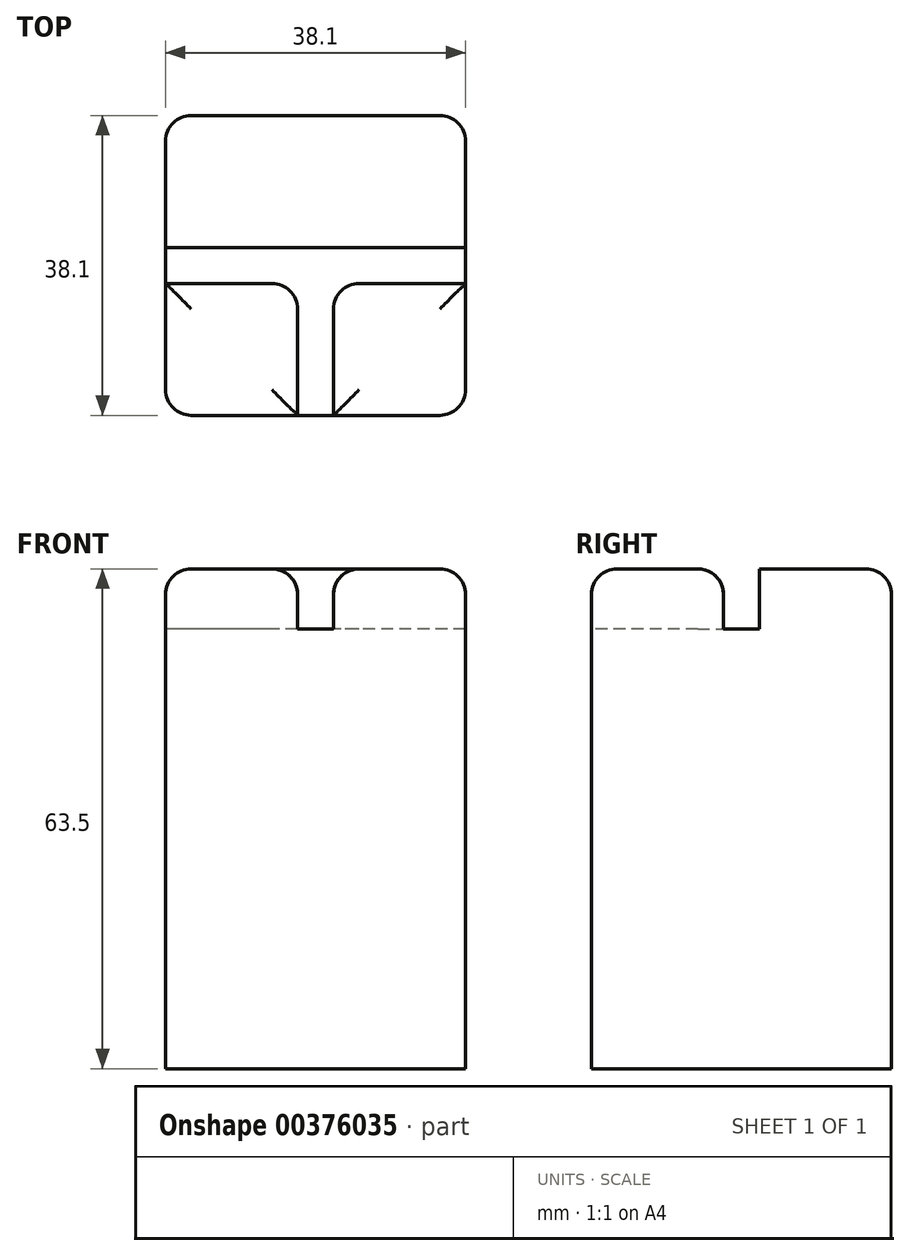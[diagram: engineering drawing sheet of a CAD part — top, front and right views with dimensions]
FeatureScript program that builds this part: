
annotation { "Feature Type Name" : "Feature", "Feature Type Description" : "" }
export const myFeature = defineFeature(function(context is Context, id is Id, definition is map)
    precondition{}
    {
        {
            var Q0;
            Q0=qCreatedBy(makeId("Top.planeOp"),FACE);
            var sketch = newSketch(context, id + "F0", { "sketchPlane" : qUnion([Q0])});
            skLineSegment(sketch, "E0.bottom", {"start": v(19.05, -19.05) * mm, "end": v(-19.05, -19.05) * mm});
            skLineSegment(sketch, "E0.top", {"start": v(19.05, 19.05) * mm, "end": v(-19.05, 19.05) * mm});
            skLineSegment(sketch, "E0.left", {"start": v(19.05, -19.05) * mm, "end": v(19.05, 19.05) * mm});
            skLineSegment(sketch, "E0.right", {"start": v(-19.05, -19.05) * mm, "end": v(-19.05, 19.05) * mm});
            skPoint(sketch, "E0.middle", {"position": v(0, 0) * mm});
            skSolve(sketch);
        }
        {
            var Q0;
            Q0=makeQuery(id+"F0.imprint","IMPRINT",FACE,{"disambiguationData":[TD([[makeQuery(id+"F0.imprint","IMPRINT",EDGE,{"derivedFrom":sQuery(id+"F0.wireOp",EDGE,"E0.bottom")}),-1.0]])]});
            var sketch = newSketch(context, id + "F1", { "sketchPlane" : qUnion([Q0])});
            skSolve(sketch);
        }
        {
            var Q0;
            Q0 = qSketchRegion(id + "F1", true);
            var Q1;
            Q1=makeQuery(id+"F0.imprint","IMPRINT",FACE,{"disambiguationData":[TD([[makeQuery(id+"F0.imprint","IMPRINT",EDGE,{"derivedFrom":sQuery(id+"F0.wireOp",EDGE,"E0.bottom")}),-1.0]])]});
            extrude(context, id + "F2", {"entities" : qUnion([Q0, Q1]), "endBound" : BoundingType.SYMMETRIC, "depth" : 63.5 * mm});
        }
        {
            var Q0;
            Q0=makeQuery(id+"F2.opExtrude","CAP_FACE",FACE,{"disambiguationData":[OSD([sQuery(id+"F0.wireOp",EDGE,"E0.bottom"),sQuery(id+"F0.wireOp",EDGE,"E0.top"),sQuery(id+"F0.wireOp",EDGE,"E0.left"),sQuery(id+"F0.wireOp",EDGE,"E0.right")])],"isStart":false});
            var sketch = newSketch(context, id + "F3", { "sketchPlane" : qUnion([Q0])});
            skLineSegment(sketch, "E1.bottom", {"start": v(19.05, -2.29) * mm, "end": v(-19.05, -2.29) * mm});
            skLineSegment(sketch, "E1.top", {"start": v(19.05, 2.29) * mm, "end": v(-19.05, 2.29) * mm});
            skLineSegment(sketch, "E1.left", {"start": v(19.05, -2.29) * mm, "end": v(19.05, 2.29) * mm});
            skLineSegment(sketch, "E1.right", {"start": v(-19.05, -2.29) * mm, "end": v(-19.05, 2.29) * mm});
            skPoint(sketch, "E1.middle", {"position": v(0, 0) * mm});
            skLineSegment(sketch, "E2.bottom", {"start": v(2.29, 19.05) * mm, "end": v(-2.29, 19.05) * mm});
            skLineSegment(sketch, "E2.top", {"start": v(2.29, -19.05) * mm, "end": v(-2.29, -19.05) * mm});
            skLineSegment(sketch, "E2.left", {"start": v(2.29, 19.05) * mm, "end": v(2.29, -19.05) * mm});
            skLineSegment(sketch, "E2.right", {"start": v(-2.29, 19.05) * mm, "end": v(-2.29, -19.05) * mm});
            skSolve(sketch);
        }
        {
            var Q0;
            {var subQ5=sQuery(id+"F3.wireOp",EDGE,"E2.bottom");Q0=makeQuery(id+"F3.imprint","IMPRINT",FACE,{"disambiguationData":[TD([[makeQuery(id+"F3.imprint","IMPRINT",EDGE,{"derivedFrom":subQ5}),1.0]])]});}
            var sketch = newSketch(context, id + "F4", { "sketchPlane" : qUnion([Q0])});
            skSolve(sketch);
        }
        {
            var Q0;
            {var subQ5=sQuery(id+"F3.wireOp",EDGE,"E2.bottom");Q0=makeQuery(id+"F4.imprint","IMPRINT",FACE,{"disambiguationData":[TD([[makeQuery(id+"F4.imprint","IMPRINT",EDGE,{"derivedFrom":makeQuery(id+"F3.imprint","IMPRINT",EDGE,{"derivedFrom":subQ5})}),1.0]])]});}
            var Q1;
            {var subQ0=sQuery(id+"F3.wireOp",EDGE,"E1.right");Q1=makeQuery(id+"F3.imprint","IMPRINT",FACE,{"disambiguationData":[TD([[makeQuery(id+"F3.imprint","IMPRINT",EDGE,{"derivedFrom":subQ0}),-1.0]])]});}
            var Q2;
            {var subQ0=sQuery(id+"F3.wireOp",EDGE,"E2.left");var subQ1=sQuery(id+"F3.wireOp",EDGE,"E1.bottom");var subQ2=makeQuery(id+"F3.imprint","INTERSECT",VERTEX,{"derivedFrom":[subQ1,subQ0]});Q2=makeQuery(id+"F3.imprint","IMPRINT",FACE,{"disambiguationData":[TD([[makeQuery(id+"F3.imprint","IMPRINT",EDGE,{"disambiguationData":[TD([[subQ2,-1.0]])],"derivedFrom":subQ1}),-1.0]])]});}
            var Q3;
            {var subQ0=sQuery(id+"F3.wireOp",EDGE,"E1.left");Q3=makeQuery(id+"F3.imprint","IMPRINT",FACE,{"disambiguationData":[TD([[makeQuery(id+"F3.imprint","IMPRINT",EDGE,{"derivedFrom":subQ0}),1.0]])]});}
            var Q4;
            {var subQ5=sQuery(id+"F3.wireOp",EDGE,"E2.top");Q4=makeQuery(id+"F3.imprint","IMPRINT",FACE,{"disambiguationData":[TD([[makeQuery(id+"F3.imprint","IMPRINT",EDGE,{"derivedFrom":subQ5}),-1.0]])]});}
            extrude(context, id + "F5", {"entities" : qUnion([Q0, Q1, Q2, Q3, Q4]), "operationType" : NewBodyOperationType.REMOVE, "oppositeDirection" : true, "depth" : 7.62 * mm});
        }
        {
            var Q0;
            {var subQ0=sQuery(id+"F0.wireOp",EDGE,"E0.left");var subQ1=sQuery(id+"F0.wireOp",EDGE,"E0.top");var subQ3=makeQuery(id+"F2.opExtrude","CAP_EDGE",EDGE,{"disambiguationData":[OSD([subQ1])],"isStart":false});Q0=makeQuery(id+"F5.boolean.opBoolean","SPLIT",EDGE,{"disambiguationData":[TD([makeQuery(id+"F2.opExtrude","SWEPT_FACE",FACE,{"disambiguationData":[OSD([subQ0])]})])],"derivedFrom":subQ3});}
            var Q1;
            {var subQ1=sQuery(id+"F0.wireOp",EDGE,"E0.left");var subQ2=sQuery(id+"F0.wireOp",EDGE,"E0.top");var subQ6=makeQuery(id+"F2.opExtrude","CAP_EDGE",EDGE,{"disambiguationData":[OSD([subQ1])],"isStart":false});Q1=makeQuery(id+"F5.boolean.opBoolean","SPLIT",EDGE,{"disambiguationData":[TD([makeQuery(id+"F2.opExtrude","SWEPT_FACE",FACE,{"disambiguationData":[OSD([subQ2])]})])],"derivedFrom":subQ6});}
            var Q2;
            Q2=makeQuery(id+"F2.opExtrude","SWEPT_EDGE",EDGE,{"disambiguationData":[OSD([sQuery(id+"F0.wireOp",EDGE,"E0.top"),sQuery(id+"F0.wireOp",EDGE,"E0.left")])]});
            var Q3;
            {var subQ0=sQuery(id+"F3.wireOp",EDGE,"E2.left");Q3=makeQuery(id+"F5.boolean.opBoolean","COPY",EDGE,{"derivedFrom":makeQuery(id+"F5.opExtrude","CAP_EDGE",EDGE,{"disambiguationData":[OSD([subQ0]),TDD([makeQuery(id+"F4.imprint","IMPRINT",EDGE,{"derivedFrom":makeQuery(id+"F3.imprint","IMPRINT",EDGE,{"disambiguationData":[TD([[makeQuery(id+"F3.imprint","INTERSECT",VERTEX,{"derivedFrom":[sQuery(id+"F3.wireOp",EDGE,"E1.top"),subQ0]}),1.0]])],"derivedFrom":subQ0})})])],"isStart":true})});}
            var Q4;
            {var subQ1=sQuery(id+"F0.wireOp",EDGE,"E0.left");var subQ3=sQuery(id+"F3.wireOp",EDGE,"E1.top");var subQ4=makeQuery(id+"F3.imprint","INTERSECT",VERTEX,{"derivedFrom":[subQ3,sQuery(id+"F3.wireOp",EDGE,"E2.right")]});var subQ5=makeQuery(id+"F3.imprint","IMPRINT",EDGE,{"disambiguationData":[TD([[subQ4,-1.0]])],"derivedFrom":subQ3});var subQ6=sQuery(id+"F3.wireOp",EDGE,"E2.left");var subQ7=makeQuery(id+"F3.imprint","INTERSECT",VERTEX,{"derivedFrom":[subQ3,subQ6]});var subQ8=makeQuery(id+"F3.imprint","IMPRINT",EDGE,{"disambiguationData":[TD([[subQ7,-1.0]])],"derivedFrom":subQ3});var subQ9=makeQuery(id+"F3.imprint","IMPRINT",EDGE,{"disambiguationData":[TD([[subQ7,1.0]])],"derivedFrom":subQ3});Q4=makeQuery(id+"F5.boolean.opBoolean","COPY",EDGE,{"disambiguationData":[TD([makeQuery(id+"F2.opExtrude","SWEPT_FACE",FACE,{"disambiguationData":[OSD([subQ1])]})])],"derivedFrom":makeQuery(id+"F5.opExtrude","CAP_EDGE",EDGE,{"disambiguationData":[OSD([subQ3]),TDD([subQ9,subQ8,subQ5])],"isStart":true})});}
            var Q5;
            Q5=makeQuery(id+"F5.boolean.opBoolean","COPY",EDGE,{"derivedFrom":makeQuery(id+"F5.opExtrude","CAP_EDGE",EDGE,{"disambiguationData":[OSD([sQuery(id+"F3.wireOp",EDGE,"E1.left")])],"isStart":false})});
            var Q6;
            Q6=makeQuery(id+"F5.boolean.opBoolean","COPY",EDGE,{"derivedFrom":makeQuery(id+"F5.opExtrude","SWEPT_EDGE",EDGE,{"disambiguationData":[OSD([sQuery(id+"F0.wireOp",EDGE,"E0.left"),sQuery(id+"F3.wireOp",EDGE,"E1.top"),sQuery(id+"F3.wireOp",EDGE,"E1.left")])]})});
            var Q7;
            Q7=makeQuery(id+"F5.boolean.opBoolean","COPY",EDGE,{"derivedFrom":makeQuery(id+"F5.opExtrude","SWEPT_EDGE",EDGE,{"disambiguationData":[OSD([sQuery(id+"F0.wireOp",EDGE,"E0.left"),sQuery(id+"F3.wireOp",EDGE,"E1.bottom"),sQuery(id+"F3.wireOp",EDGE,"E1.left")])]})});
            var Q8;
            {var subQ0=sQuery(id+"F0.wireOp",EDGE,"E0.bottom");var subQ2=sQuery(id+"F0.wireOp",EDGE,"E0.left");var subQ3=makeQuery(id+"F2.opExtrude","CAP_EDGE",EDGE,{"disambiguationData":[OSD([subQ2])],"isStart":false});Q8=makeQuery(id+"F5.boolean.opBoolean","SPLIT",EDGE,{"disambiguationData":[TD([makeQuery(id+"F2.opExtrude","SWEPT_FACE",FACE,{"disambiguationData":[OSD([subQ0])]})])],"derivedFrom":subQ3});}
            var Q9;
            Q9=makeQuery(id+"F2.opExtrude","SWEPT_EDGE",EDGE,{"disambiguationData":[OSD([sQuery(id+"F0.wireOp",EDGE,"E0.bottom"),sQuery(id+"F0.wireOp",EDGE,"E0.left")])]});
            var Q10;
            {var subQ0=sQuery(id+"F0.wireOp",EDGE,"E0.bottom");var subQ1=sQuery(id+"F0.wireOp",EDGE,"E0.left");var subQ3=makeQuery(id+"F2.opExtrude","CAP_EDGE",EDGE,{"disambiguationData":[OSD([subQ0])],"isStart":false});Q10=makeQuery(id+"F5.boolean.opBoolean","SPLIT",EDGE,{"disambiguationData":[TD([makeQuery(id+"F2.opExtrude","SWEPT_FACE",FACE,{"disambiguationData":[OSD([subQ1])]})])],"derivedFrom":subQ3});}
            var Q11;
            Q11=makeQuery(id+"F5.boolean.opBoolean","COPY",EDGE,{"derivedFrom":makeQuery(id+"F5.opExtrude","SWEPT_EDGE",EDGE,{"disambiguationData":[OSD([sQuery(id+"F0.wireOp",EDGE,"E0.bottom"),sQuery(id+"F3.wireOp",EDGE,"E2.top"),sQuery(id+"F3.wireOp",EDGE,"E2.left")])]})});
            var Q12;
            Q12=makeQuery(id+"F5.boolean.opBoolean","COPY",EDGE,{"derivedFrom":makeQuery(id+"F5.opExtrude","CAP_EDGE",EDGE,{"disambiguationData":[OSD([sQuery(id+"F3.wireOp",EDGE,"E2.top")])],"isStart":false})});
            var Q13;
            Q13=makeQuery(id+"F5.boolean.opBoolean","COPY",EDGE,{"derivedFrom":makeQuery(id+"F5.opExtrude","SWEPT_EDGE",EDGE,{"disambiguationData":[OSD([sQuery(id+"F0.wireOp",EDGE,"E0.bottom"),sQuery(id+"F3.wireOp",EDGE,"E2.top"),sQuery(id+"F3.wireOp",EDGE,"E2.right")])]})});
            var Q14;
            {var subQ0=sQuery(id+"F3.wireOp",EDGE,"E2.left");Q14=makeQuery(id+"F5.boolean.opBoolean","COPY",EDGE,{"derivedFrom":makeQuery(id+"F5.opExtrude","CAP_EDGE",EDGE,{"disambiguationData":[OSD([subQ0]),TDD([makeQuery(id+"F3.imprint","IMPRINT",EDGE,{"disambiguationData":[TD([[makeQuery(id+"F3.imprint","INTERSECT",VERTEX,{"derivedFrom":[sQuery(id+"F3.wireOp",EDGE,"E1.bottom"),subQ0]}),-1.0]])],"derivedFrom":subQ0})])],"isStart":true})});}
            var Q15;
            {var subQ0=sQuery(id+"F3.wireOp",EDGE,"E1.bottom");Q15=makeQuery(id+"F5.boolean.opBoolean","COPY",EDGE,{"derivedFrom":makeQuery(id+"F5.opExtrude","CAP_EDGE",EDGE,{"disambiguationData":[OSD([subQ0]),TDD([makeQuery(id+"F3.imprint","IMPRINT",EDGE,{"disambiguationData":[TD([[makeQuery(id+"F3.imprint","INTERSECT",VERTEX,{"derivedFrom":[subQ0,sQuery(id+"F3.wireOp",EDGE,"E2.left")]}),1.0]])],"derivedFrom":subQ0})])],"isStart":true})});}
            var Q16;
            {var subQ0=sQuery(id+"F0.wireOp",EDGE,"E0.bottom");var subQ1=sQuery(id+"F0.wireOp",EDGE,"E0.right");var subQ2=sQuery(id+"F3.wireOp",EDGE,"E1.bottom");var subQ3=sQuery(id+"F3.wireOp",EDGE,"E2.right");var subQ4=makeQuery(id+"F3.imprint","INTERSECT",VERTEX,{"derivedFrom":[subQ2,subQ3]});Q16=makeQuery(id+"F5.boolean.opBoolean","SPLIT",FACE,{"disambiguationData":[TD([makeQuery(id+"F5.opExtrude","SWEPT_FACE",FACE,{"disambiguationData":[OSD([subQ2]),TDD([makeQuery(id+"F3.imprint","IMPRINT",EDGE,{"disambiguationData":[TD([[subQ4,-1.0]])],"derivedFrom":subQ2})])]})])],"derivedFrom":makeQuery(id+"F2.opExtrude","CAP_FACE",FACE,{"disambiguationData":[OSD([subQ0,sQuery(id+"F0.wireOp",EDGE,"E0.top"),sQuery(id+"F0.wireOp",EDGE,"E0.left"),subQ1])],"isStart":false})});}
            var Q17;
            {var subQ0=sQuery(id+"F3.wireOp",EDGE,"E1.bottom");Q17=makeQuery(id+"F5.boolean.opBoolean","COPY",EDGE,{"derivedFrom":makeQuery(id+"F5.opExtrude","CAP_EDGE",EDGE,{"disambiguationData":[OSD([subQ0]),TDD([makeQuery(id+"F3.imprint","IMPRINT",EDGE,{"disambiguationData":[TD([[makeQuery(id+"F3.imprint","INTERSECT",VERTEX,{"derivedFrom":[subQ0,sQuery(id+"F3.wireOp",EDGE,"E2.right")]}),-1.0]])],"derivedFrom":subQ0})])],"isStart":true})});}
            var Q18;
            Q18=makeQuery(id+"F5.boolean.opBoolean","COPY",EDGE,{"derivedFrom":makeQuery(id+"F5.opExtrude","SWEPT_EDGE",EDGE,{"disambiguationData":[OSD([sQuery(id+"F0.wireOp",EDGE,"E0.right"),sQuery(id+"F3.wireOp",EDGE,"E1.bottom"),sQuery(id+"F3.wireOp",EDGE,"E1.right")])]})});
            var Q19;
            Q19=makeQuery(id+"F5.boolean.opBoolean","COPY",EDGE,{"derivedFrom":makeQuery(id+"F5.opExtrude","CAP_EDGE",EDGE,{"disambiguationData":[OSD([sQuery(id+"F3.wireOp",EDGE,"E1.right")])],"isStart":false})});
            var Q20;
            Q20=makeQuery(id+"F5.boolean.opBoolean","COPY",EDGE,{"derivedFrom":makeQuery(id+"F5.opExtrude","SWEPT_EDGE",EDGE,{"disambiguationData":[OSD([sQuery(id+"F0.wireOp",EDGE,"E0.right"),sQuery(id+"F3.wireOp",EDGE,"E1.top"),sQuery(id+"F3.wireOp",EDGE,"E1.right")])]})});
            var Q21;
            {var subQ0=sQuery(id+"F0.wireOp",EDGE,"E0.right");var subQ2=sQuery(id+"F0.wireOp",EDGE,"E0.top");var subQ4=makeQuery(id+"F2.opExtrude","CAP_EDGE",EDGE,{"disambiguationData":[OSD([subQ0])],"isStart":false});Q21=makeQuery(id+"F5.boolean.opBoolean","SPLIT",EDGE,{"disambiguationData":[TD([makeQuery(id+"F2.opExtrude","SWEPT_FACE",FACE,{"disambiguationData":[OSD([subQ2])]})])],"derivedFrom":subQ4});}
            var Q22;
            Q22=makeQuery(id+"F2.opExtrude","SWEPT_EDGE",EDGE,{"disambiguationData":[OSD([sQuery(id+"F0.wireOp",EDGE,"E0.top"),sQuery(id+"F0.wireOp",EDGE,"E0.right")])]});
            var Q23;
            {var subQ0=sQuery(id+"F0.wireOp",EDGE,"E0.right");var subQ1=sQuery(id+"F0.wireOp",EDGE,"E0.top");var subQ3=makeQuery(id+"F2.opExtrude","CAP_EDGE",EDGE,{"disambiguationData":[OSD([subQ1])],"isStart":false});Q23=makeQuery(id+"F5.boolean.opBoolean","SPLIT",EDGE,{"disambiguationData":[TD([makeQuery(id+"F2.opExtrude","SWEPT_FACE",FACE,{"disambiguationData":[OSD([subQ0])]})])],"derivedFrom":subQ3});}
            var Q24;
            {var subQ0=sQuery(id+"F0.wireOp",EDGE,"E0.right");var subQ3=sQuery(id+"F3.wireOp",EDGE,"E2.right");var subQ4=sQuery(id+"F3.wireOp",EDGE,"E1.top");var subQ5=makeQuery(id+"F3.imprint","INTERSECT",VERTEX,{"derivedFrom":[subQ4,subQ3]});var subQ6=makeQuery(id+"F3.imprint","IMPRINT",EDGE,{"disambiguationData":[TD([[subQ5,-1.0]])],"derivedFrom":subQ4});var subQ7=makeQuery(id+"F3.imprint","INTERSECT",VERTEX,{"derivedFrom":[subQ4,sQuery(id+"F3.wireOp",EDGE,"E2.left")]});var subQ8=makeQuery(id+"F3.imprint","IMPRINT",EDGE,{"disambiguationData":[TD([[subQ7,-1.0]])],"derivedFrom":subQ4});var subQ9=makeQuery(id+"F3.imprint","IMPRINT",EDGE,{"disambiguationData":[TD([[subQ7,1.0]])],"derivedFrom":subQ4});Q24=makeQuery(id+"F5.boolean.opBoolean","COPY",EDGE,{"disambiguationData":[TD([makeQuery(id+"F2.opExtrude","SWEPT_FACE",FACE,{"disambiguationData":[OSD([subQ0])]})])],"derivedFrom":makeQuery(id+"F5.opExtrude","CAP_EDGE",EDGE,{"disambiguationData":[OSD([subQ4]),TDD([subQ9,subQ8,subQ6])],"isStart":true})});}
            var Q25;
            {var subQ0=sQuery(id+"F3.wireOp",EDGE,"E2.right");Q25=makeQuery(id+"F5.boolean.opBoolean","COPY",EDGE,{"derivedFrom":makeQuery(id+"F5.opExtrude","CAP_EDGE",EDGE,{"disambiguationData":[OSD([subQ0]),TDD([makeQuery(id+"F4.imprint","IMPRINT",EDGE,{"derivedFrom":makeQuery(id+"F3.imprint","IMPRINT",EDGE,{"disambiguationData":[TD([[makeQuery(id+"F3.imprint","INTERSECT",VERTEX,{"derivedFrom":[sQuery(id+"F3.wireOp",EDGE,"E1.top"),subQ0]}),1.0]])],"derivedFrom":subQ0})})])],"isStart":true})});}
            var Q26;
            {var subQ0=sQuery(id+"F0.wireOp",EDGE,"E0.bottom");var subQ1=sQuery(id+"F0.wireOp",EDGE,"E0.right");var subQ3=makeQuery(id+"F2.opExtrude","CAP_EDGE",EDGE,{"disambiguationData":[OSD([subQ1])],"isStart":false});Q26=makeQuery(id+"F5.boolean.opBoolean","SPLIT",EDGE,{"disambiguationData":[TD([makeQuery(id+"F2.opExtrude","SWEPT_FACE",FACE,{"disambiguationData":[OSD([subQ0])]})])],"derivedFrom":subQ3});}
            var Q27;
            {var subQ0=sQuery(id+"F0.wireOp",EDGE,"E0.bottom");var subQ1=sQuery(id+"F0.wireOp",EDGE,"E0.right");var subQ3=makeQuery(id+"F2.opExtrude","CAP_EDGE",EDGE,{"disambiguationData":[OSD([subQ0])],"isStart":false});Q27=makeQuery(id+"F5.boolean.opBoolean","SPLIT",EDGE,{"disambiguationData":[TD([makeQuery(id+"F2.opExtrude","SWEPT_FACE",FACE,{"disambiguationData":[OSD([subQ1])]})])],"derivedFrom":subQ3});}
            var Q28;
            Q28=makeQuery(id+"F5.boolean.opBoolean","COPY",EDGE,{"derivedFrom":makeQuery(id+"F5.opExtrude","SWEPT_EDGE",EDGE,{"disambiguationData":[OSD([sQuery(id+"F3.wireOp",EDGE,"E2.bottom"),sQuery(id+"F3.wireOp",EDGE,"E2.right")])]})});
            var Q29;
            Q29=makeQuery(id+"F5.boolean.opBoolean","COPY",EDGE,{"derivedFrom":makeQuery(id+"F5.opExtrude","SWEPT_EDGE",EDGE,{"disambiguationData":[OSD([sQuery(id+"F3.wireOp",EDGE,"E2.bottom"),sQuery(id+"F3.wireOp",EDGE,"E2.left")])]})});
            var Q30;
            Q30=makeQuery(id+"F5.boolean.opBoolean","COPY",EDGE,{"derivedFrom":makeQuery(id+"F5.opExtrude","CAP_EDGE",EDGE,{"disambiguationData":[OSD([sQuery(id+"F3.wireOp",EDGE,"E2.bottom")])],"isStart":false})});
            var Q31;
            Q31=makeQuery(id+"F5.boolean.opBoolean","COPY",EDGE,{"derivedFrom":makeQuery(id+"F5.opExtrude","SWEPT_EDGE",EDGE,{"disambiguationData":[OSD([sQuery(id+"F3.wireOp",EDGE,"E1.top"),sQuery(id+"F3.wireOp",EDGE,"E2.right")])]})});
            var Q32;
            Q32=makeQuery(id+"F5.boolean.opBoolean","COPY",EDGE,{"derivedFrom":makeQuery(id+"F5.opExtrude","SWEPT_EDGE",EDGE,{"disambiguationData":[OSD([sQuery(id+"F3.wireOp",EDGE,"E1.bottom"),sQuery(id+"F3.wireOp",EDGE,"E2.right")])]})});
            var Q33;
            Q33=makeQuery(id+"F5.boolean.opBoolean","COPY",EDGE,{"derivedFrom":makeQuery(id+"F5.opExtrude","SWEPT_EDGE",EDGE,{"disambiguationData":[OSD([sQuery(id+"F3.wireOp",EDGE,"E1.top"),sQuery(id+"F3.wireOp",EDGE,"E2.left")])]})});
            var Q34;
            Q34=makeQuery(id+"F5.boolean.opBoolean","COPY",EDGE,{"derivedFrom":makeQuery(id+"F5.opExtrude","SWEPT_EDGE",EDGE,{"disambiguationData":[OSD([sQuery(id+"F3.wireOp",EDGE,"E1.bottom"),sQuery(id+"F3.wireOp",EDGE,"E2.left")])]})});
            var Q35;
            Q35=makeQuery(id+"F2.opExtrude","SWEPT_EDGE",EDGE,{"disambiguationData":[OSD([sQuery(id+"F0.wireOp",EDGE,"E0.bottom"),sQuery(id+"F0.wireOp",EDGE,"E0.right")])]});
            fillet(context, id + "F6", {"entities" : qUnion([Q0, Q1, Q2, Q3, Q4, Q5, Q6, Q7, Q8, Q9, Q10, Q11, Q12, Q13, Q14, Q15, Q16, Q17, Q18, Q19, Q20, Q21, Q22, Q23, Q24, Q25, Q26, Q27, Q28, Q29, Q30, Q31, Q32, Q33, Q34, Q35]), "radius" : 3.26 * mm, "tangentPropagation" : true, "allowEdgeOverflow" : false});
        }
    });
